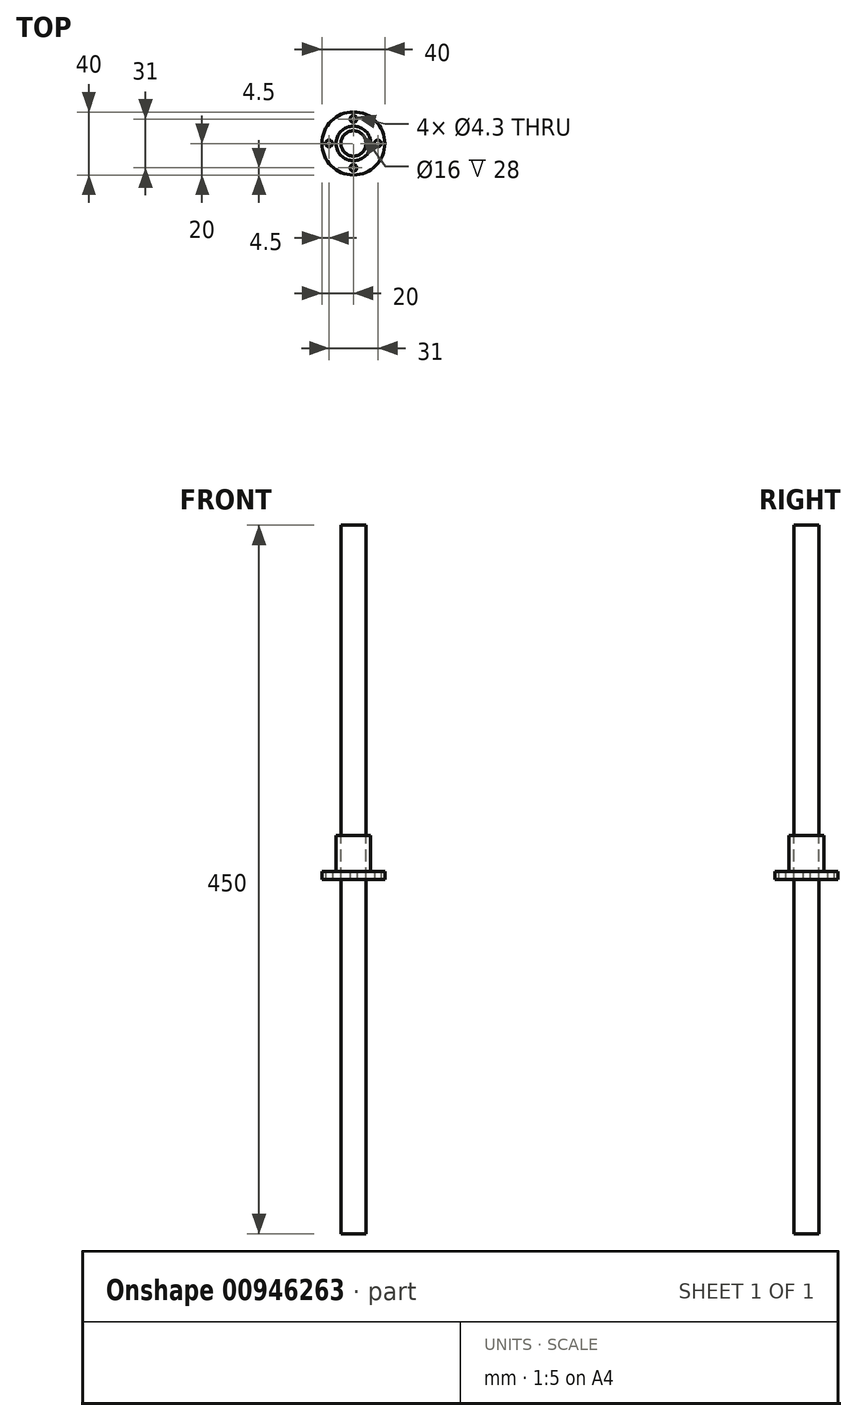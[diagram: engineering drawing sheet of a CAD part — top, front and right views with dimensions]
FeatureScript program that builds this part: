
annotation { "Feature Type Name" : "Feature", "Feature Type Description" : "" }
export const myFeature = defineFeature(function(context is Context, id is Id, definition is map)
    precondition{}
    {
        {
            var Q0;
            Q0=qCreatedBy(makeId("Front.planeOp"),FACE);
            var sketch = newSketch(context, id + "F0", { "sketchPlane" : qUnion([Q0])});
            skLineSegment(sketch, "E0", {"start": v(0, 0) * mm, "end": v(-20, 0) * mm});
            skLineSegment(sketch, "E1", {"start": v(-20, 0) * mm, "end": v(-20, 5) * mm});
            skLineSegment(sketch, "E2", {"start": v(-20, 5) * mm, "end": v(-11, 5) * mm});
            skLineSegment(sketch, "E3", {"start": v(-11, 5) * mm, "end": v(-11, 28) * mm});
            skLineSegment(sketch, "E4", {"start": v(-11, 28) * mm, "end": v(0, 28) * mm});
            skLineSegment(sketch, "E5", {"start": v(0, 28) * mm, "end": v(0, 0) * mm});
            skSolve(sketch);
        }
        {
            var Q0;
            Q0=makeQuery(id+"F0.imprint","IMPRINT",FACE,{"disambiguationData":[TD([[makeQuery(id+"F0.imprint","IMPRINT",EDGE,{"derivedFrom":sQuery(id+"F0.wireOp",EDGE,"E0")}),-1.0]])]});
            var Q1;
            Q1=sQuery(id+"F0.wireOp",EDGE,"E5");
            revolve(context, id + "F1", {"surfaceOperationType" : NewSurfaceOperationType.NEW, "entities" : qUnion([Q0]), "axis" : qUnion([Q1]), "revolveType" : RevolveType.FULL});
        }
        {
            var Q0;
            Q0=makeQuery(id+"F1.opRevolve","SWEPT_FACE",FACE,{"disambiguationData":[OSD([sQuery(id+"F0.wireOp",EDGE,"E0")])]});
            var sketch = newSketch(context, id + "F2", { "sketchPlane" : qUnion([Q0])});
            skPoint(sketch, "E6", {"position": v(0, 0) * mm});
            skCircle(sketch, "E7", {"center": v(0, 0) * mm, "radius": 15.5 * mm, "construction": true});
            skLineSegment(sketch, "E8", {"start": v(0, 18.55) * mm, "end": v(0, -18.18) * mm, "construction": true});
            skLineSegment(sketch, "E9", {"start": v(-17.6, 0) * mm, "end": v(18, 0) * mm, "construction": true});
            skPoint(sketch, "E10", {"position": v(0, 15.5) * mm});
            skPoint(sketch, "E11", {"position": v(-15.5, 0) * mm});
            skPoint(sketch, "E12", {"position": v(0, -15.5) * mm});
            skPoint(sketch, "E13", {"position": v(15.5, 0) * mm});
            skSolve(sketch);
        }
        {
            var Q0;
            Q0=sQuery(id+"F2.wireOp",VERTEX,"E6");
            var Q1;
            Q1=makeQuery(id+"F1.opRevolve","SWEPT_BODY",BODY,{"disambiguationData":[OSD([sQuery(id+"F0.wireOp",EDGE,"E0"),sQuery(id+"F0.wireOp",EDGE,"E1"),sQuery(id+"F0.wireOp",EDGE,"E2"),sQuery(id+"F0.wireOp",EDGE,"E3"),sQuery(id+"F0.wireOp",EDGE,"E4"),sQuery(id+"F0.wireOp",EDGE,"E5")])]});
            hole(context, id + "F3", {"style" : HoleStyle.SIMPLE, "endStyle" : HoleEndStyle.THROUGH, "holeDiameter" : 16 * mm, "majorDiameter" : 5 * mm, "isTappedThrough" : true, "tappedDepth" : 14.3 * mm, "tapClearance" : 3, "locations" : qUnion([Q0]), "scope" : qUnion([Q1])});
        }
        {
            var Q0;
            Q0=sQuery(id+"F2.wireOp",VERTEX,"E10");
            var Q1;
            Q1=sQuery(id+"F2.wireOp",VERTEX,"E13");
            var Q2;
            Q2=sQuery(id+"F2.wireOp",VERTEX,"E12");
            var Q3;
            Q3=sQuery(id+"F2.wireOp",VERTEX,"E11");
            var Q4;
            Q4=makeQuery(id+"F1.opRevolve","SWEPT_BODY",BODY,{"disambiguationData":[OSD([sQuery(id+"F0.wireOp",EDGE,"E0"),sQuery(id+"F0.wireOp",EDGE,"E1"),sQuery(id+"F0.wireOp",EDGE,"E2"),sQuery(id+"F0.wireOp",EDGE,"E3"),sQuery(id+"F0.wireOp",EDGE,"E4"),sQuery(id+"F0.wireOp",EDGE,"E5")])]});
            hole(context, id + "F4", {"style" : HoleStyle.SIMPLE, "endStyle" : HoleEndStyle.THROUGH, "holeDiameter" : 4.3 * mm, "majorDiameter" : 5 * mm, "isTappedThrough" : true, "tappedDepth" : 14.3 * mm, "tapClearance" : 3, "locations" : qUnion([Q0, Q1, Q2, Q3]), "scope" : qUnion([Q4])});
        }
        {
            var Q0;
            Q0=makeQuery(id+"F1.opRevolve","SWEPT_FACE",FACE,{"disambiguationData":[OSD([sQuery(id+"F0.wireOp",EDGE,"E0")])]});
            var sketch = newSketch(context, id + "F5", { "sketchPlane" : qUnion([Q0])});
            skCircle(sketch, "E14.0", {"center": v(0, 0) * mm, "radius": 8 * mm});
            skSolve(sketch);
        }
        {
            var Q0;
            Q0 = qSketchRegion(id + "F5", true);
            extrude(context, id + "F6", {"entities" : qUnion([Q0]), "depth" : 225 * mm, "offsetDistance" : 25 * mm, "hasSecondDirection" : true, "secondDirectionOppositeDirection" : true, "secondDirectionDepth" : 225 * mm});
        }
    });
